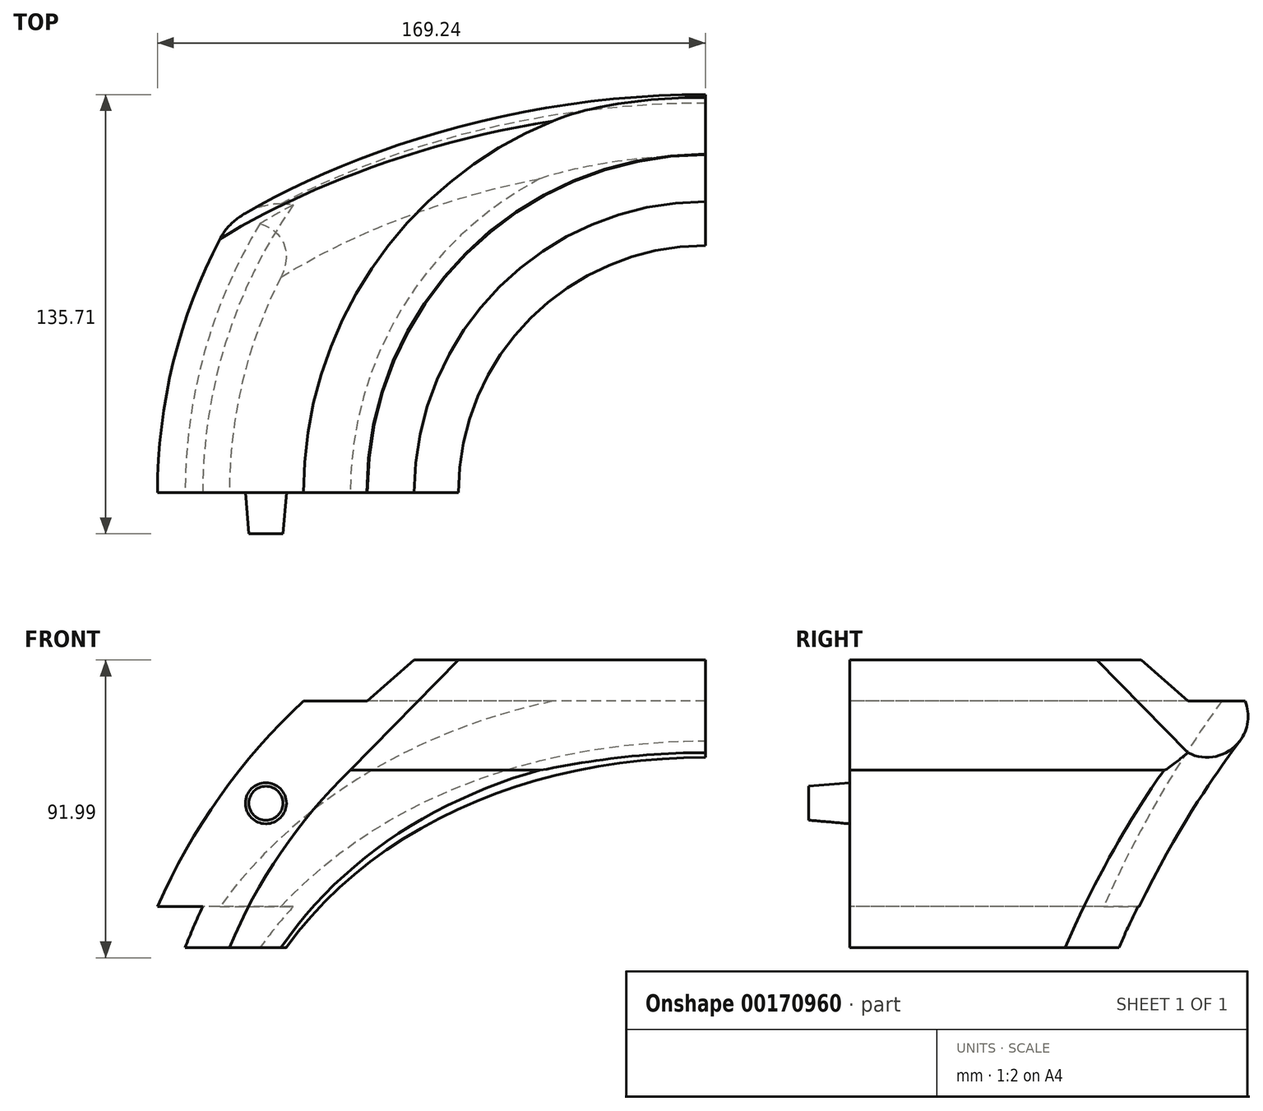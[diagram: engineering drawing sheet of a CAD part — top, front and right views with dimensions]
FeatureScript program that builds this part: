
annotation { "Feature Type Name" : "Feature", "Feature Type Description" : "" }
export const myFeature = defineFeature(function(context is Context, id is Id, definition is map)
    precondition{}
    {
        {
            var Q0;
            Q0=qCreatedBy(makeId("Front.planeOp"),FACE);
            var sketch = newSketch(context, id + "F0", { "sketchPlane" : qUnion([Q0])});
            skArc(sketch, "E0", {"start": v(-129.52, 139.7) * mm, "mid": v(-155.34, 110.28) * mm, "end": v(-174.6, 76.2) * mm});
            skArc(sketch, "E1", {"start": v(-160.64, 76.2) * mm, "mid": v(-163.48, 69.9) * mm, "end": v(-166.07, 63.5) * mm});
            skLineSegment(sketch, "E2", {"start": v(-5.36, 76.2) * mm, "end": v(-146.46, 76.2) * mm});
            skLineSegment(sketch, "E3", {"start": v(-5.36, 152.4) * mm, "end": v(-95.3, 152.4) * mm});
            skArc(sketch, "E4", {"start": v(-115.03, 118.43) * mm, "mid": v(-136.5, 92.86) * mm, "end": v(-152.4, 63.5) * mm});
            skLineSegment(sketch, "E5", {"start": v(-166.07, 63.5) * mm, "end": v(-152.4, 63.5) * mm});
            skLineSegment(sketch, "E6", {"start": v(-174.6, 76.2) * mm, "end": v(-160.64, 76.2) * mm});
            skLineSegment(sketch, "E7", {"start": v(-129.52, 139.7) * mm, "end": v(-109.99, 139.7) * mm});
            skLineSegment(sketch, "E8", {"start": v(-5.36, 152.4) * mm, "end": v(-5.36, 76.2) * mm});
            skLineSegment(sketch, "E9", {"start": v(-81.67, 152.4) * mm, "end": v(-115.03, 118.43) * mm});
            skLineSegment(sketch, "E10", {"start": v(-95.3, 152.4) * mm, "end": v(-109.77, 139.7) * mm});
            skLineSegment(sketch, "E11", {"start": v(-109.77, 139.7) * mm, "end": v(-109.99, 139.7) * mm});
            skPoint(sketch, "E12.orphan", {"position": v(-91.58, 152.4) * mm});
            skSolve(sketch);
        }
        {
            var Q0;
            Q0=makeQuery(id+"F0.imprint","IMPRINT",FACE,{"disambiguationData":[TD([[makeQuery(id+"F0.imprint","IMPRINT",EDGE,{"derivedFrom":sQuery(id+"F0.wireOp",EDGE,"E0")}),1.0]])]});
            var Q1;
            Q1=sQuery(id+"F0.wireOp",EDGE,"E8");
            revolve(context, id + "F1", {"entities" : qUnion([Q0]), "axis" : qUnion([Q1]), "revolveType" : RevolveType.ONE_DIRECTION, "angle" : 90 * degree});
        }
        {
            var Q0;
            Q0=qCreatedBy(makeId("Right.planeOp"),FACE);
            var sketch = newSketch(context, id + "F2", { "sketchPlane" : qUnion([Q0])});
            skCircle(sketch, "E13", {"center": v(368.31, -58.28) * mm, "radius": 309.68 * mm});
            skSolve(sketch);
        }
        {
            var Q0;
            Q0 = qSketchRegion(id + "F2", true);
            extrude(context, id + "F3", {"entities" : qUnion([Q0]), "operationType" : NewBodyOperationType.REMOVE, "endBound" : BoundingType.THROUGH_ALL, "oppositeDirection" : true, "depth" : 25.4 * mm});
        }
        {
            var Q0;
            Q0=makeQuery(id+"F3.boolean.opBoolean","INTERSECT",EDGE,{"derivedFrom":[makeQuery(id+"F1.opRevolve","SWEPT_FACE",FACE,{"disambiguationData":[OSD([sQuery(id+"F0.wireOp",EDGE,"E0")])]}),makeQuery(id+"F3.opExtrude","SWEPT_FACE",FACE,{"disambiguationData":[OSD([sQuery(id+"F2.wireOp",EDGE,"E13")])]})]});
            var Q1;
            Q1=makeQuery(id+"F3.boolean.opBoolean","INTERSECT",EDGE,{"derivedFrom":[makeQuery(id+"F1.opRevolve","SWEPT_FACE",FACE,{"disambiguationData":[OSD([sQuery(id+"F0.wireOp",EDGE,"E4")])]}),makeQuery(id+"F3.opExtrude","SWEPT_FACE",FACE,{"disambiguationData":[OSD([sQuery(id+"F2.wireOp",EDGE,"E13")])]})]});
            fillet(context, id + "F4", {"entities" : qUnion([Q0, Q1]), "radius" : 12.7 * mm, "tangentPropagation" : true, "allowEdgeOverflow" : false});
        }
        {
            var Q0;
            Q0=makeQuery(id+"F1.opRevolve","CAP_FACE",FACE,{"disambiguationData":[OSD([sQuery(id+"F0.wireOp",EDGE,"E0"),sQuery(id+"F0.wireOp",EDGE,"E1"),sQuery(id+"F0.wireOp",EDGE,"E3"),sQuery(id+"F0.wireOp",EDGE,"E4"),sQuery(id+"F0.wireOp",EDGE,"E5"),sQuery(id+"F0.wireOp",EDGE,"E6"),sQuery(id+"F0.wireOp",EDGE,"E7"),sQuery(id+"F0.wireOp",EDGE,"E9"),sQuery(id+"F0.wireOp",EDGE,"E10"),sQuery(id+"F0.wireOp",EDGE,"E11")])],"isStart":true});
            var sketch = newSketch(context, id + "F5", { "sketchPlane" : qUnion([Q0])});
            skCircle(sketch, "E14", {"center": v(-141.12, 108.16) * mm, "radius": 6.35 * mm});
            skSolve(sketch);
        }
        {
            var Q0;
            Q0=makeQuery(id+"F5.imprint","IMPRINT",FACE,{"disambiguationData":[TD([[makeQuery(id+"F5.imprint","IMPRINT",EDGE,{"derivedFrom":sQuery(id+"F5.wireOp",EDGE,"E14")}),1.0]])]});
            var Q1;
            Q1=sQuery(id+"F5.wireOp",EDGE,"E14");
            extrude(context, id + "F6", {"entities" : qUnion([Q0]), "operationType" : NewBodyOperationType.ADD, "surfaceEntities" : qUnion([Q1]), "depth" : 12.7 * mm, "hasDraft" : true, "draftAngle" : 5 * degree, "draftPullDirection" : true});
        }
    });
